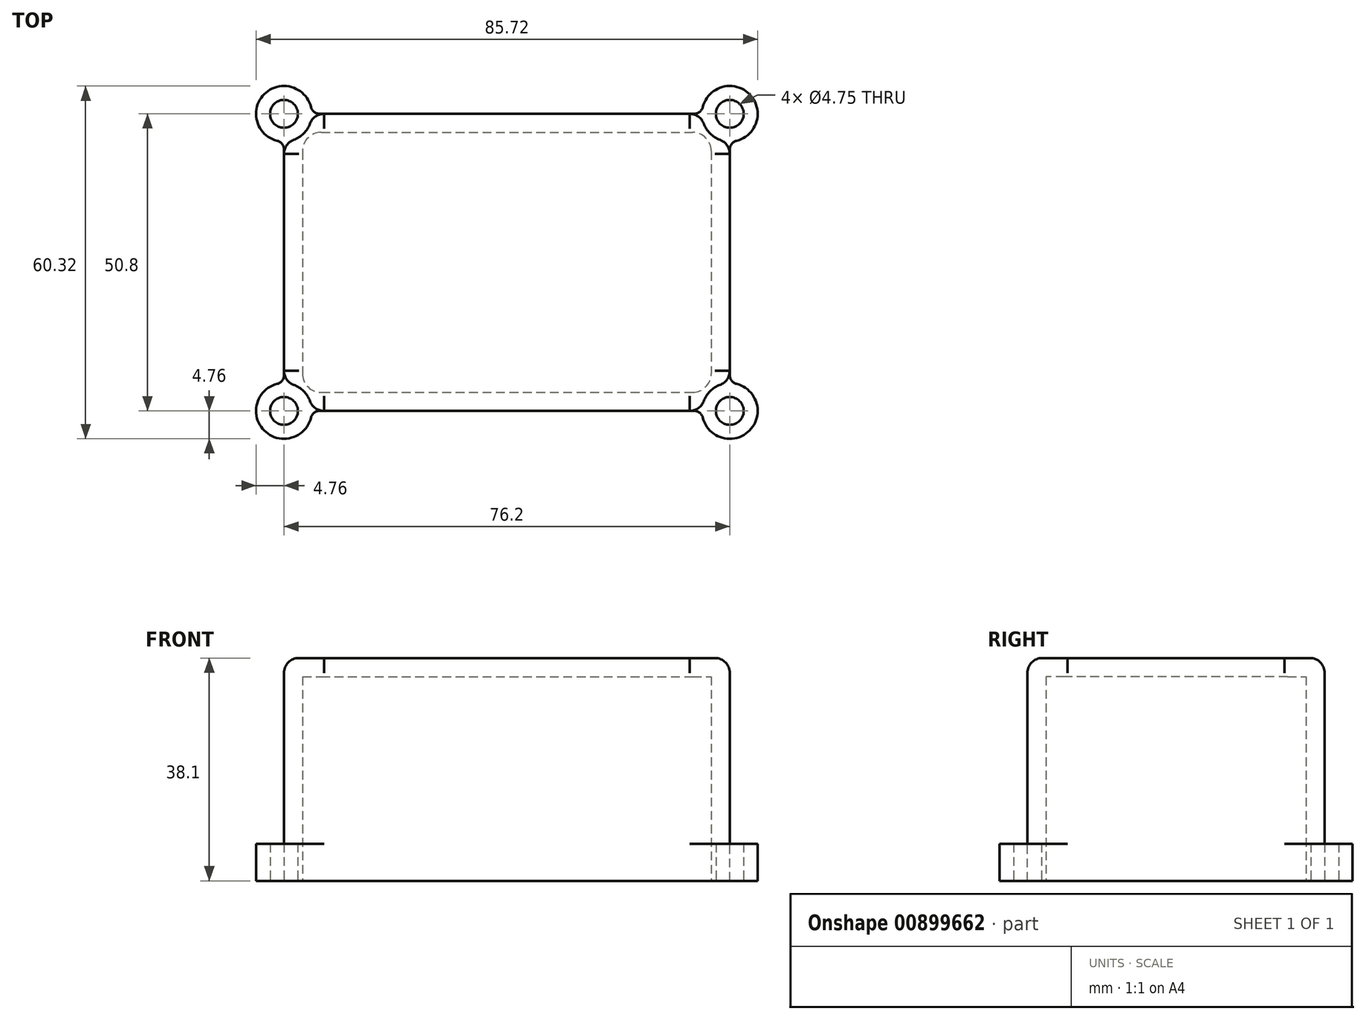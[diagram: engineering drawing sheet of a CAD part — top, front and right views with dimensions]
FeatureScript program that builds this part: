
annotation { "Feature Type Name" : "Feature", "Feature Type Description" : "" }
export const myFeature = defineFeature(function(context is Context, id is Id, definition is map)
    precondition{}
    {
        {
            var Q0;
            Q0=qCreatedBy(makeId("Front.planeOp"),FACE);
            var sketch = newSketch(context, id + "F0", { "sketchPlane" : qUnion([Q0])});
            skLineSegment(sketch, "E0.bottom", {"start": v(0, 0) * mm, "end": v(76.2, 0) * mm});
            skLineSegment(sketch, "E0.top", {"start": v(0, 38.1) * mm, "end": v(76.2, 38.1) * mm});
            skLineSegment(sketch, "E0.left", {"start": v(0, 0) * mm, "end": v(0, 38.1) * mm});
            skLineSegment(sketch, "E0.right", {"start": v(76.2, 0) * mm, "end": v(76.2, 38.1) * mm});
            skSolve(sketch);
        }
        {
            var Q0;
            Q0=makeQuery(id+"F0.imprint","IMPRINT",FACE,{"disambiguationData":[TD([[makeQuery(id+"F0.imprint","IMPRINT",EDGE,{"derivedFrom":sQuery(id+"F0.wireOp",EDGE,"E0.bottom")}),1.0]])]});
            extrude(context, id + "F1", {"entities" : qUnion([Q0]), "oppositeDirection" : true, "depth" : 50.8 * mm, "offsetDistance" : 25.4 * mm});
        }
        {
            var Q0;
            Q0=makeQuery(id+"F1.opExtrude","SWEPT_FACE",FACE,{"disambiguationData":[OSD([sQuery(id+"F0.wireOp",EDGE,"E0.bottom")])]});
            var sketch = newSketch(context, id + "F2", { "sketchPlane" : qUnion([Q0])});
            skCircle(sketch, "E1", {"center": v(76.2, 0) * mm, "radius": 4.76 * mm});
            skCircle(sketch, "E2", {"center": v(0, 0) * mm, "radius": 4.76 * mm});
            skCircle(sketch, "E3", {"center": v(0, -50.8) * mm, "radius": 4.76 * mm});
            skCircle(sketch, "E4", {"center": v(76.2, -50.8) * mm, "radius": 4.76 * mm});
            skSolve(sketch);
        }
        {
            var Q0;
            {var subQ0=sQuery(id+"F2.wireOp",EDGE,"E2");var subQ1=sQuery(id+"F0.wireOp",EDGE,"E0.bottom");var subQ4=makeQuery(id+"F1.opExtrude","CAP_EDGE",EDGE,{"disambiguationData":[OSD([subQ1])],"isStart":true});var subQ5=makeQuery(id+"F2.imprint","INTERSECT",VERTEX,{"derivedFrom":[subQ4,subQ0]});Q0=makeQuery(id+"F2.imprint","IMPRINT",FACE,{"disambiguationData":[TD([[makeQuery(id+"F2.imprint","IMPRINT",EDGE,{"disambiguationData":[TD([[subQ5,-1.0]])],"derivedFrom":subQ0}),1.0]])]});}
            var Q1;
            {var subQ0=sQuery(id+"F2.wireOp",EDGE,"E1");var subQ1=sQuery(id+"F0.wireOp",EDGE,"E0.bottom");var subQ4=makeQuery(id+"F1.opExtrude","CAP_EDGE",EDGE,{"disambiguationData":[OSD([subQ1])],"isStart":true});var subQ5=makeQuery(id+"F2.imprint","INTERSECT",VERTEX,{"derivedFrom":[subQ4,subQ0]});Q1=makeQuery(id+"F2.imprint","IMPRINT",FACE,{"disambiguationData":[TD([[makeQuery(id+"F2.imprint","IMPRINT",EDGE,{"disambiguationData":[TD([[subQ5,1.0]])],"derivedFrom":subQ0}),1.0]])]});}
            var Q2;
            {var subQ0=sQuery(id+"F2.wireOp",EDGE,"E4");var subQ1=sQuery(id+"F0.wireOp",EDGE,"E0.bottom");var subQ4=makeQuery(id+"F1.opExtrude","CAP_EDGE",EDGE,{"disambiguationData":[OSD([subQ1])],"isStart":false});var subQ5=makeQuery(id+"F2.imprint","INTERSECT",VERTEX,{"derivedFrom":[subQ4,subQ0]});Q2=makeQuery(id+"F2.imprint","IMPRINT",FACE,{"disambiguationData":[TD([[makeQuery(id+"F2.imprint","IMPRINT",EDGE,{"disambiguationData":[TD([[subQ5,-1.0]])],"derivedFrom":subQ0}),1.0]])]});}
            var Q3;
            {var subQ0=sQuery(id+"F2.wireOp",EDGE,"E3");var subQ1=sQuery(id+"F0.wireOp",EDGE,"E0.bottom");var subQ4=makeQuery(id+"F1.opExtrude","CAP_EDGE",EDGE,{"disambiguationData":[OSD([subQ1])],"isStart":false});var subQ5=makeQuery(id+"F2.imprint","INTERSECT",VERTEX,{"derivedFrom":[subQ4,subQ0]});Q3=makeQuery(id+"F2.imprint","IMPRINT",FACE,{"disambiguationData":[TD([[makeQuery(id+"F2.imprint","IMPRINT",EDGE,{"disambiguationData":[TD([[subQ5,1.0]])],"derivedFrom":subQ0}),1.0]])]});}
            var Q4;
            {var subQ0=sQuery(id+"F2.wireOp",EDGE,"E2");var subQ1=sQuery(id+"F0.wireOp",EDGE,"E0.bottom");var subQ4=makeQuery(id+"F1.opExtrude","CAP_EDGE",EDGE,{"disambiguationData":[OSD([subQ1])],"isStart":true});var subQ5=makeQuery(id+"F2.imprint","INTERSECT",VERTEX,{"derivedFrom":[subQ4,subQ0]});Q4=makeQuery(id+"F2.imprint","IMPRINT",FACE,{"disambiguationData":[TD([[makeQuery(id+"F2.imprint","IMPRINT",EDGE,{"disambiguationData":[TD([[subQ5,1.0]])],"derivedFrom":subQ0}),1.0]])]});}
            var Q5;
            {var subQ0=sQuery(id+"F2.wireOp",EDGE,"E1");var subQ1=sQuery(id+"F0.wireOp",EDGE,"E0.bottom");var subQ4=makeQuery(id+"F1.opExtrude","CAP_EDGE",EDGE,{"disambiguationData":[OSD([subQ1])],"isStart":true});var subQ5=makeQuery(id+"F2.imprint","INTERSECT",VERTEX,{"derivedFrom":[subQ4,subQ0]});Q5=makeQuery(id+"F2.imprint","IMPRINT",FACE,{"disambiguationData":[TD([[makeQuery(id+"F2.imprint","IMPRINT",EDGE,{"disambiguationData":[TD([[subQ5,-1.0]])],"derivedFrom":subQ0}),1.0]])]});}
            var Q6;
            {var subQ0=sQuery(id+"F2.wireOp",EDGE,"E4");var subQ1=sQuery(id+"F0.wireOp",EDGE,"E0.bottom");var subQ4=makeQuery(id+"F1.opExtrude","CAP_EDGE",EDGE,{"disambiguationData":[OSD([subQ1])],"isStart":false});var subQ5=makeQuery(id+"F2.imprint","INTERSECT",VERTEX,{"derivedFrom":[subQ4,subQ0]});Q6=makeQuery(id+"F2.imprint","IMPRINT",FACE,{"disambiguationData":[TD([[makeQuery(id+"F2.imprint","IMPRINT",EDGE,{"disambiguationData":[TD([[subQ5,1.0]])],"derivedFrom":subQ0}),1.0]])]});}
            var Q7;
            {var subQ0=sQuery(id+"F2.wireOp",EDGE,"E3");var subQ1=sQuery(id+"F0.wireOp",EDGE,"E0.bottom");var subQ4=makeQuery(id+"F1.opExtrude","CAP_EDGE",EDGE,{"disambiguationData":[OSD([subQ1])],"isStart":false});var subQ5=makeQuery(id+"F2.imprint","INTERSECT",VERTEX,{"derivedFrom":[subQ4,subQ0]});Q7=makeQuery(id+"F2.imprint","IMPRINT",FACE,{"disambiguationData":[TD([[makeQuery(id+"F2.imprint","IMPRINT",EDGE,{"disambiguationData":[TD([[subQ5,-1.0]])],"derivedFrom":subQ0}),1.0]])]});}
            extrude(context, id + "F3", {"entities" : qUnion([Q0, Q1, Q2, Q3, Q4, Q5, Q6, Q7]), "operationType" : NewBodyOperationType.ADD, "oppositeDirection" : true, "depth" : 6.35 * mm, "offsetDistance" : 25.4 * mm});
        }
        {
            var Q0;
            Q0=makeQuery(id+"F1.opExtrude","SWEPT_FACE",FACE,{"disambiguationData":[OSD([sQuery(id+"F0.wireOp",EDGE,"E0.top")])]});
            var sketch = newSketch(context, id + "F4", { "sketchPlane" : qUnion([Q0])});
            skCircle(sketch, "E5", {"center": v(76.2, 50.8) * mm, "radius": 4.76 * mm});
            skCircle(sketch, "E6", {"center": v(76.2, 0) * mm, "radius": 4.76 * mm});
            skCircle(sketch, "E7", {"center": v(0, 0) * mm, "radius": 4.76 * mm});
            skCircle(sketch, "E8", {"center": v(0, 50.8) * mm, "radius": 4.76 * mm});
            skSolve(sketch);
        }
        {
            var Q0;
            {var subQ0=sQuery(id+"F4.wireOp",EDGE,"E5");var subQ1=sQuery(id+"F0.wireOp",EDGE,"E0.top");var subQ4=makeQuery(id+"F1.opExtrude","CAP_EDGE",EDGE,{"disambiguationData":[OSD([subQ1])],"isStart":false});var subQ5=makeQuery(id+"F4.imprint","INTERSECT",VERTEX,{"derivedFrom":[subQ4,subQ0]});Q0=makeQuery(id+"F4.imprint","IMPRINT",FACE,{"disambiguationData":[TD([[makeQuery(id+"F4.imprint","IMPRINT",EDGE,{"disambiguationData":[TD([[subQ5,-1.0]])],"derivedFrom":subQ0}),1.0]])]});}
            var Q1;
            {var subQ0=sQuery(id+"F4.wireOp",EDGE,"E5");var subQ1=sQuery(id+"F0.wireOp",EDGE,"E0.top");var subQ4=makeQuery(id+"F1.opExtrude","CAP_EDGE",EDGE,{"disambiguationData":[OSD([subQ1])],"isStart":false});var subQ5=makeQuery(id+"F4.imprint","INTERSECT",VERTEX,{"derivedFrom":[subQ4,subQ0]});Q1=makeQuery(id+"F4.imprint","IMPRINT",FACE,{"disambiguationData":[TD([[makeQuery(id+"F4.imprint","IMPRINT",EDGE,{"disambiguationData":[TD([[subQ5,1.0]])],"derivedFrom":subQ0}),1.0]])]});}
            var Q2;
            {var subQ0=sQuery(id+"F4.wireOp",EDGE,"E6");var subQ1=sQuery(id+"F0.wireOp",EDGE,"E0.top");var subQ4=makeQuery(id+"F1.opExtrude","CAP_EDGE",EDGE,{"disambiguationData":[OSD([subQ1])],"isStart":true});var subQ5=makeQuery(id+"F4.imprint","INTERSECT",VERTEX,{"derivedFrom":[subQ4,subQ0]});Q2=makeQuery(id+"F4.imprint","IMPRINT",FACE,{"disambiguationData":[TD([[makeQuery(id+"F4.imprint","IMPRINT",EDGE,{"disambiguationData":[TD([[subQ5,-1.0]])],"derivedFrom":subQ0}),1.0]])]});}
            var Q3;
            {var subQ0=sQuery(id+"F4.wireOp",EDGE,"E6");var subQ1=sQuery(id+"F0.wireOp",EDGE,"E0.top");var subQ4=makeQuery(id+"F1.opExtrude","CAP_EDGE",EDGE,{"disambiguationData":[OSD([subQ1])],"isStart":true});var subQ5=makeQuery(id+"F4.imprint","INTERSECT",VERTEX,{"derivedFrom":[subQ4,subQ0]});Q3=makeQuery(id+"F4.imprint","IMPRINT",FACE,{"disambiguationData":[TD([[makeQuery(id+"F4.imprint","IMPRINT",EDGE,{"disambiguationData":[TD([[subQ5,1.0]])],"derivedFrom":subQ0}),1.0]])]});}
            var Q4;
            {var subQ0=sQuery(id+"F4.wireOp",EDGE,"E8");var subQ1=sQuery(id+"F0.wireOp",EDGE,"E0.top");var subQ4=makeQuery(id+"F1.opExtrude","CAP_EDGE",EDGE,{"disambiguationData":[OSD([subQ1])],"isStart":false});var subQ5=makeQuery(id+"F4.imprint","INTERSECT",VERTEX,{"derivedFrom":[subQ4,subQ0]});Q4=makeQuery(id+"F4.imprint","IMPRINT",FACE,{"disambiguationData":[TD([[makeQuery(id+"F4.imprint","IMPRINT",EDGE,{"disambiguationData":[TD([[subQ5,1.0]])],"derivedFrom":subQ0}),1.0]])]});}
            var Q5;
            {var subQ0=sQuery(id+"F4.wireOp",EDGE,"E8");var subQ1=sQuery(id+"F0.wireOp",EDGE,"E0.top");var subQ4=makeQuery(id+"F1.opExtrude","CAP_EDGE",EDGE,{"disambiguationData":[OSD([subQ1])],"isStart":false});var subQ5=makeQuery(id+"F4.imprint","INTERSECT",VERTEX,{"derivedFrom":[subQ4,subQ0]});Q5=makeQuery(id+"F4.imprint","IMPRINT",FACE,{"disambiguationData":[TD([[makeQuery(id+"F4.imprint","IMPRINT",EDGE,{"disambiguationData":[TD([[subQ5,-1.0]])],"derivedFrom":subQ0}),1.0]])]});}
            var Q6;
            {var subQ0=sQuery(id+"F4.wireOp",EDGE,"E7");var subQ1=sQuery(id+"F0.wireOp",EDGE,"E0.top");var subQ4=makeQuery(id+"F1.opExtrude","CAP_EDGE",EDGE,{"disambiguationData":[OSD([subQ1])],"isStart":true});var subQ5=makeQuery(id+"F4.imprint","INTERSECT",VERTEX,{"derivedFrom":[subQ4,subQ0]});Q6=makeQuery(id+"F4.imprint","IMPRINT",FACE,{"disambiguationData":[TD([[makeQuery(id+"F4.imprint","IMPRINT",EDGE,{"disambiguationData":[TD([[subQ5,1.0]])],"derivedFrom":subQ0}),1.0]])]});}
            var Q7;
            {var subQ0=sQuery(id+"F4.wireOp",EDGE,"E7");var subQ1=sQuery(id+"F0.wireOp",EDGE,"E0.top");var subQ4=makeQuery(id+"F1.opExtrude","CAP_EDGE",EDGE,{"disambiguationData":[OSD([subQ1])],"isStart":true});var subQ5=makeQuery(id+"F4.imprint","INTERSECT",VERTEX,{"derivedFrom":[subQ4,subQ0]});Q7=makeQuery(id+"F4.imprint","IMPRINT",FACE,{"disambiguationData":[TD([[makeQuery(id+"F4.imprint","IMPRINT",EDGE,{"disambiguationData":[TD([[subQ5,-1.0]])],"derivedFrom":subQ0}),1.0]])]});}
            var Q8;
            Q8=makeQuery(id+"F3.opExtrude","CAP_FACE",FACE,{"disambiguationData":[OSD([sQuery(id+"F2.wireOp",EDGE,"E3")])],"isStart":false});
            extrude(context, id + "F5", {"entities" : qUnion([Q0, Q1, Q2, Q3, Q4, Q5, Q6, Q7]), "operationType" : NewBodyOperationType.REMOVE, "endBound" : BoundingType.UP_TO_SURFACE, "oppositeDirection" : true, "depth" : 25.4 * mm, "endBoundEntityFace" : qUnion([Q8]), "offsetDistance" : 25.4 * mm});
        }
        {
            var Q0;
            Q0=makeQuery(id+"F3.boolean.opBoolean","MERGE",FACE,{"derivedFrom":[makeQuery(id+"F1.opExtrude","SWEPT_FACE",FACE,{"disambiguationData":[OSD([sQuery(id+"F0.wireOp",EDGE,"E0.bottom")])]}),makeQuery(id+"F3.opExtrude","CAP_FACE",FACE,{"disambiguationData":[OSD([sQuery(id+"F2.wireOp",EDGE,"E1")])],"isStart":true}),makeQuery(id+"F3.opExtrude","CAP_FACE",FACE,{"disambiguationData":[OSD([sQuery(id+"F2.wireOp",EDGE,"E2")])],"isStart":true}),makeQuery(id+"F3.opExtrude","CAP_FACE",FACE,{"disambiguationData":[OSD([sQuery(id+"F2.wireOp",EDGE,"E3")])],"isStart":true}),makeQuery(id+"F3.opExtrude","CAP_FACE",FACE,{"disambiguationData":[OSD([sQuery(id+"F2.wireOp",EDGE,"E4")])],"isStart":true})]});
            var sketch = newSketch(context, id + "F6", { "sketchPlane" : qUnion([Q0])});
            skLineSegment(sketch, "E9.0", {"start": v(6.35, -47.63) * mm, "end": v(69.85, -47.63) * mm});
            skLineSegment(sketch, "E10.0", {"start": v(3.18, -44.45) * mm, "end": v(3.18, -6.35) * mm});
            skLineSegment(sketch, "E11.0", {"start": v(6.35, -3.18) * mm, "end": v(69.85, -3.18) * mm});
            skLineSegment(sketch, "E12.0", {"start": v(73.03, -44.45) * mm, "end": v(73.03, -6.35) * mm});
            skLineSegment(sketch, "E13.filletArc", {"start": v(73.03, -47.63) * mm, "end": v(73.03, -47.63) * mm});
            skLineSegment(sketch, "E14.filletArc", {"start": v(3.18, -47.63) * mm, "end": v(3.18, -47.63) * mm});
            skLineSegment(sketch, "E15.filletArc", {"start": v(3.17, -3.18) * mm, "end": v(3.17, -3.18) * mm});
            skLineSegment(sketch, "E16.filletArc", {"start": v(73.03, -3.18) * mm, "end": v(73.03, -3.18) * mm});
            skArc(sketch, "E17.filletArc", {"start": v(69.85, -47.63) * mm, "mid": v(72.1, -46.7) * mm, "end": v(73.03, -44.45) * mm});
            skArc(sketch, "E18.filletArc", {"start": v(3.18, -44.45) * mm, "mid": v(4.1, -46.7) * mm, "end": v(6.35, -47.63) * mm});
            skPoint(sketch, "E19.visualSharp", {"position": v(3.18, -3.18) * mm});
            skArc(sketch, "E19.filletArc", {"start": v(6.35, -3.18) * mm, "mid": v(4.1, -4.1) * mm, "end": v(3.18, -6.35) * mm});
            skArc(sketch, "E20.filletArc", {"start": v(73.03, -6.35) * mm, "mid": v(72.1, -4.1) * mm, "end": v(69.85, -3.17) * mm});
            skSolve(sketch);
        }
        {
            var Q0;
            Q0=makeQuery(id+"F6.imprint","IMPRINT",FACE,{"disambiguationData":[TD([[makeQuery(id+"F6.imprint","IMPRINT",EDGE,{"derivedFrom":sQuery(id+"F6.wireOp",EDGE,"E9.0")}),1.0]])]});
            extrude(context, id + "F7", {"entities" : qUnion([Q0]), "operationType" : NewBodyOperationType.REMOVE, "oppositeDirection" : true, "depth" : 34.92 * mm, "offsetDistance" : 25.4 * mm});
        }
        {
            var Q0;
            Q0=makeQuery(id+"F3.boolean.opBoolean","MERGE",FACE,{"derivedFrom":[makeQuery(id+"F1.opExtrude","SWEPT_FACE",FACE,{"disambiguationData":[OSD([sQuery(id+"F0.wireOp",EDGE,"E0.bottom")])]}),makeQuery(id+"F3.opExtrude","CAP_FACE",FACE,{"disambiguationData":[OSD([sQuery(id+"F2.wireOp",EDGE,"E1")])],"isStart":true}),makeQuery(id+"F3.opExtrude","CAP_FACE",FACE,{"disambiguationData":[OSD([sQuery(id+"F2.wireOp",EDGE,"E2")])],"isStart":true}),makeQuery(id+"F3.opExtrude","CAP_FACE",FACE,{"disambiguationData":[OSD([sQuery(id+"F2.wireOp",EDGE,"E3")])],"isStart":true}),makeQuery(id+"F3.opExtrude","CAP_FACE",FACE,{"disambiguationData":[OSD([sQuery(id+"F2.wireOp",EDGE,"E4")])],"isStart":true})]});
            var sketch = newSketch(context, id + "F8", { "sketchPlane" : qUnion([Q0])});
            skCircle(sketch, "E21", {"center": v(76.2, -50.8) * mm, "radius": 2.37 * mm});
            skCircle(sketch, "E22", {"center": v(0, -50.8) * mm, "radius": 2.37 * mm});
            skCircle(sketch, "E23", {"center": v(0, 0) * mm, "radius": 2.37 * mm});
            skCircle(sketch, "E24", {"center": v(76.2, 0) * mm, "radius": 2.37 * mm});
            skSolve(sketch);
        }
        {
            var Q0;
            Q0=makeQuery(id+"F8.imprint","IMPRINT",FACE,{"disambiguationData":[TD([[makeQuery(id+"F8.imprint","IMPRINT",EDGE,{"derivedFrom":sQuery(id+"F8.wireOp",EDGE,"E24")}),1.0]])]});
            var Q1;
            Q1=makeQuery(id+"F8.imprint","IMPRINT",FACE,{"disambiguationData":[TD([[makeQuery(id+"F8.imprint","IMPRINT",EDGE,{"derivedFrom":sQuery(id+"F8.wireOp",EDGE,"E21")}),1.0]])]});
            var Q2;
            Q2=makeQuery(id+"F8.imprint","IMPRINT",FACE,{"disambiguationData":[TD([[makeQuery(id+"F8.imprint","IMPRINT",EDGE,{"derivedFrom":sQuery(id+"F8.wireOp",EDGE,"E22")}),1.0]])]});
            var Q3;
            Q3=makeQuery(id+"F8.imprint","IMPRINT",FACE,{"disambiguationData":[TD([[makeQuery(id+"F8.imprint","IMPRINT",EDGE,{"derivedFrom":sQuery(id+"F8.wireOp",EDGE,"E23")}),1.0]])]});
            extrude(context, id + "F9", {"entities" : qUnion([Q0, Q1, Q2, Q3]), "operationType" : NewBodyOperationType.REMOVE, "oppositeDirection" : true, "depth" : 9.52 * mm, "offsetDistance" : 25.4 * mm});
        }
        {
            var Q0;
            Q0=makeQuery(id+"F1.opExtrude","CAP_EDGE",EDGE,{"disambiguationData":[OSD([sQuery(id+"F0.wireOp",EDGE,"E0.top")])],"isStart":true});
            var Q1;
            Q1=makeQuery(id+"F1.opExtrude","SWEPT_EDGE",EDGE,{"disambiguationData":[OSD([sQuery(id+"F0.wireOp",EDGE,"E0.top"),sQuery(id+"F0.wireOp",EDGE,"E0.right")])]});
            var Q2;
            Q2=makeQuery(id+"F5.boolean.opBoolean","COPY",EDGE,{"derivedFrom":makeQuery(id+"F5.opExtrude","CAP_EDGE",EDGE,{"disambiguationData":[OSD([sQuery(id+"F4.wireOp",EDGE,"E6")])],"isStart":true})});
            var Q3;
            Q3=makeQuery(id+"F5.boolean.opBoolean","COPY",EDGE,{"derivedFrom":makeQuery(id+"F5.opExtrude","CAP_EDGE",EDGE,{"disambiguationData":[OSD([sQuery(id+"F4.wireOp",EDGE,"E5")])],"isStart":true})});
            var Q4;
            Q4=makeQuery(id+"F1.opExtrude","CAP_EDGE",EDGE,{"disambiguationData":[OSD([sQuery(id+"F0.wireOp",EDGE,"E0.top")])],"isStart":false});
            var Q5;
            Q5=makeQuery(id+"F1.opExtrude","SWEPT_EDGE",EDGE,{"disambiguationData":[OSD([sQuery(id+"F0.wireOp",EDGE,"E0.top"),sQuery(id+"F0.wireOp",EDGE,"E0.left")])]});
            var Q6;
            Q6=makeQuery(id+"F5.boolean.opBoolean","COPY",EDGE,{"derivedFrom":makeQuery(id+"F5.opExtrude","CAP_EDGE",EDGE,{"disambiguationData":[OSD([sQuery(id+"F4.wireOp",EDGE,"E8")])],"isStart":true})});
            var Q7;
            Q7=makeQuery(id+"F5.boolean.opBoolean","COPY",EDGE,{"derivedFrom":makeQuery(id+"F5.opExtrude","CAP_EDGE",EDGE,{"disambiguationData":[OSD([sQuery(id+"F4.wireOp",EDGE,"E7")])],"isStart":true})});
            fillet(context, id + "F10", {"entities" : qUnion([Q0, Q1, Q2, Q3, Q4, Q5, Q6, Q7]), "radius" : 2.54 * mm, "tangentPropagation" : true, "allowEdgeOverflow" : false});
        }
        {
            var Q0;
            Q0=makeQuery(id+"F5.boolean.opBoolean","INTERSECT",EDGE,{"derivedFrom":[makeQuery(id+"F1.opExtrude","CAP_FACE",FACE,{"disambiguationData":[OSD([sQuery(id+"F0.wireOp",EDGE,"E0.bottom"),sQuery(id+"F0.wireOp",EDGE,"E0.top"),sQuery(id+"F0.wireOp",EDGE,"E0.left"),sQuery(id+"F0.wireOp",EDGE,"E0.right")])],"isStart":false}),makeQuery(id+"F5.opExtrude","SWEPT_FACE",FACE,{"disambiguationData":[OSD([sQuery(id+"F4.wireOp",EDGE,"E5")])]})]});
            var Q1;
            Q1=makeQuery(id+"F5.boolean.opBoolean","INTERSECT",EDGE,{"derivedFrom":[makeQuery(id+"F1.opExtrude","SWEPT_FACE",FACE,{"disambiguationData":[OSD([sQuery(id+"F0.wireOp",EDGE,"E0.right")])]}),makeQuery(id+"F5.opExtrude","SWEPT_FACE",FACE,{"disambiguationData":[OSD([sQuery(id+"F4.wireOp",EDGE,"E5")])]})]});
            var Q2;
            Q2=makeQuery(id+"F5.boolean.opBoolean","INTERSECT",EDGE,{"derivedFrom":[makeQuery(id+"F1.opExtrude","CAP_FACE",FACE,{"disambiguationData":[OSD([sQuery(id+"F0.wireOp",EDGE,"E0.bottom"),sQuery(id+"F0.wireOp",EDGE,"E0.top"),sQuery(id+"F0.wireOp",EDGE,"E0.left"),sQuery(id+"F0.wireOp",EDGE,"E0.right")])],"isStart":false}),makeQuery(id+"F5.opExtrude","SWEPT_FACE",FACE,{"disambiguationData":[OSD([sQuery(id+"F4.wireOp",EDGE,"E8")])]})]});
            var Q3;
            Q3=makeQuery(id+"F5.boolean.opBoolean","INTERSECT",EDGE,{"derivedFrom":[makeQuery(id+"F1.opExtrude","SWEPT_FACE",FACE,{"disambiguationData":[OSD([sQuery(id+"F0.wireOp",EDGE,"E0.left")])]}),makeQuery(id+"F5.opExtrude","SWEPT_FACE",FACE,{"disambiguationData":[OSD([sQuery(id+"F4.wireOp",EDGE,"E8")])]})]});
            var Q4;
            Q4=makeQuery(id+"F5.boolean.opBoolean","INTERSECT",EDGE,{"derivedFrom":[makeQuery(id+"F1.opExtrude","CAP_FACE",FACE,{"disambiguationData":[OSD([sQuery(id+"F0.wireOp",EDGE,"E0.bottom"),sQuery(id+"F0.wireOp",EDGE,"E0.top"),sQuery(id+"F0.wireOp",EDGE,"E0.left"),sQuery(id+"F0.wireOp",EDGE,"E0.right")])],"isStart":true}),makeQuery(id+"F5.opExtrude","SWEPT_FACE",FACE,{"disambiguationData":[OSD([sQuery(id+"F4.wireOp",EDGE,"E7")])]})]});
            var Q5;
            Q5=makeQuery(id+"F5.boolean.opBoolean","INTERSECT",EDGE,{"derivedFrom":[makeQuery(id+"F1.opExtrude","SWEPT_FACE",FACE,{"disambiguationData":[OSD([sQuery(id+"F0.wireOp",EDGE,"E0.left")])]}),makeQuery(id+"F5.opExtrude","SWEPT_FACE",FACE,{"disambiguationData":[OSD([sQuery(id+"F4.wireOp",EDGE,"E7")])]})]});
            var Q6;
            Q6=makeQuery(id+"F5.boolean.opBoolean","INTERSECT",EDGE,{"derivedFrom":[makeQuery(id+"F1.opExtrude","SWEPT_FACE",FACE,{"disambiguationData":[OSD([sQuery(id+"F0.wireOp",EDGE,"E0.right")])]}),makeQuery(id+"F5.opExtrude","SWEPT_FACE",FACE,{"disambiguationData":[OSD([sQuery(id+"F4.wireOp",EDGE,"E6")])]})]});
            var Q7;
            Q7=makeQuery(id+"F5.boolean.opBoolean","INTERSECT",EDGE,{"derivedFrom":[makeQuery(id+"F1.opExtrude","CAP_FACE",FACE,{"disambiguationData":[OSD([sQuery(id+"F0.wireOp",EDGE,"E0.bottom"),sQuery(id+"F0.wireOp",EDGE,"E0.top"),sQuery(id+"F0.wireOp",EDGE,"E0.left"),sQuery(id+"F0.wireOp",EDGE,"E0.right")])],"isStart":true}),makeQuery(id+"F5.opExtrude","SWEPT_FACE",FACE,{"disambiguationData":[OSD([sQuery(id+"F4.wireOp",EDGE,"E6")])]})]});
            fillet(context, id + "F11", {"entities" : qUnion([Q0, Q1, Q2, Q3, Q4, Q5, Q6, Q7]), "radius" : 2.54 * mm, "tangentPropagation" : true, "allowEdgeOverflow" : false});
        }
        {
            var Q0;
            Q0=makeQuery(id+"F3.boolean.opBoolean","INTERSECT",EDGE,{"derivedFrom":[makeQuery(id+"F1.opExtrude","CAP_FACE",FACE,{"disambiguationData":[OSD([sQuery(id+"F0.wireOp",EDGE,"E0.bottom"),sQuery(id+"F0.wireOp",EDGE,"E0.top"),sQuery(id+"F0.wireOp",EDGE,"E0.left"),sQuery(id+"F0.wireOp",EDGE,"E0.right")])],"isStart":true}),makeQuery(id+"F3.opExtrude","SWEPT_FACE",FACE,{"disambiguationData":[OSD([sQuery(id+"F2.wireOp",EDGE,"E1")])]})]});
            var Q1;
            Q1=makeQuery(id+"F3.boolean.opBoolean","INTERSECT",EDGE,{"derivedFrom":[makeQuery(id+"F1.opExtrude","SWEPT_FACE",FACE,{"disambiguationData":[OSD([sQuery(id+"F0.wireOp",EDGE,"E0.right")])]}),makeQuery(id+"F3.opExtrude","SWEPT_FACE",FACE,{"disambiguationData":[OSD([sQuery(id+"F2.wireOp",EDGE,"E1")])]})]});
            var Q2;
            Q2=makeQuery(id+"F3.boolean.opBoolean","INTERSECT",EDGE,{"derivedFrom":[makeQuery(id+"F1.opExtrude","SWEPT_FACE",FACE,{"disambiguationData":[OSD([sQuery(id+"F0.wireOp",EDGE,"E0.right")])]}),makeQuery(id+"F3.opExtrude","SWEPT_FACE",FACE,{"disambiguationData":[OSD([sQuery(id+"F2.wireOp",EDGE,"E4")])]})]});
            var Q3;
            Q3=makeQuery(id+"F3.boolean.opBoolean","INTERSECT",EDGE,{"derivedFrom":[makeQuery(id+"F1.opExtrude","CAP_FACE",FACE,{"disambiguationData":[OSD([sQuery(id+"F0.wireOp",EDGE,"E0.bottom"),sQuery(id+"F0.wireOp",EDGE,"E0.top"),sQuery(id+"F0.wireOp",EDGE,"E0.left"),sQuery(id+"F0.wireOp",EDGE,"E0.right")])],"isStart":false}),makeQuery(id+"F3.opExtrude","SWEPT_FACE",FACE,{"disambiguationData":[OSD([sQuery(id+"F2.wireOp",EDGE,"E4")])]})]});
            var Q4;
            Q4=makeQuery(id+"F3.boolean.opBoolean","INTERSECT",EDGE,{"derivedFrom":[makeQuery(id+"F1.opExtrude","CAP_FACE",FACE,{"disambiguationData":[OSD([sQuery(id+"F0.wireOp",EDGE,"E0.bottom"),sQuery(id+"F0.wireOp",EDGE,"E0.top"),sQuery(id+"F0.wireOp",EDGE,"E0.left"),sQuery(id+"F0.wireOp",EDGE,"E0.right")])],"isStart":false}),makeQuery(id+"F3.opExtrude","SWEPT_FACE",FACE,{"disambiguationData":[OSD([sQuery(id+"F2.wireOp",EDGE,"E3")])]})]});
            var Q5;
            Q5=makeQuery(id+"F3.boolean.opBoolean","INTERSECT",EDGE,{"derivedFrom":[makeQuery(id+"F1.opExtrude","SWEPT_FACE",FACE,{"disambiguationData":[OSD([sQuery(id+"F0.wireOp",EDGE,"E0.left")])]}),makeQuery(id+"F3.opExtrude","SWEPT_FACE",FACE,{"disambiguationData":[OSD([sQuery(id+"F2.wireOp",EDGE,"E3")])]})]});
            var Q6;
            Q6=makeQuery(id+"F3.boolean.opBoolean","INTERSECT",EDGE,{"derivedFrom":[makeQuery(id+"F1.opExtrude","SWEPT_FACE",FACE,{"disambiguationData":[OSD([sQuery(id+"F0.wireOp",EDGE,"E0.left")])]}),makeQuery(id+"F3.opExtrude","SWEPT_FACE",FACE,{"disambiguationData":[OSD([sQuery(id+"F2.wireOp",EDGE,"E2")])]})]});
            var Q7;
            Q7=makeQuery(id+"F3.boolean.opBoolean","INTERSECT",EDGE,{"derivedFrom":[makeQuery(id+"F1.opExtrude","CAP_FACE",FACE,{"disambiguationData":[OSD([sQuery(id+"F0.wireOp",EDGE,"E0.bottom"),sQuery(id+"F0.wireOp",EDGE,"E0.top"),sQuery(id+"F0.wireOp",EDGE,"E0.left"),sQuery(id+"F0.wireOp",EDGE,"E0.right")])],"isStart":true}),makeQuery(id+"F3.opExtrude","SWEPT_FACE",FACE,{"disambiguationData":[OSD([sQuery(id+"F2.wireOp",EDGE,"E2")])]})]});
            fillet(context, id + "F12", {"entities" : qUnion([Q0, Q1, Q2, Q3, Q4, Q5, Q6, Q7]), "radius" : 1.52 * mm, "tangentPropagation" : true, "allowEdgeOverflow" : false});
        }
    });
